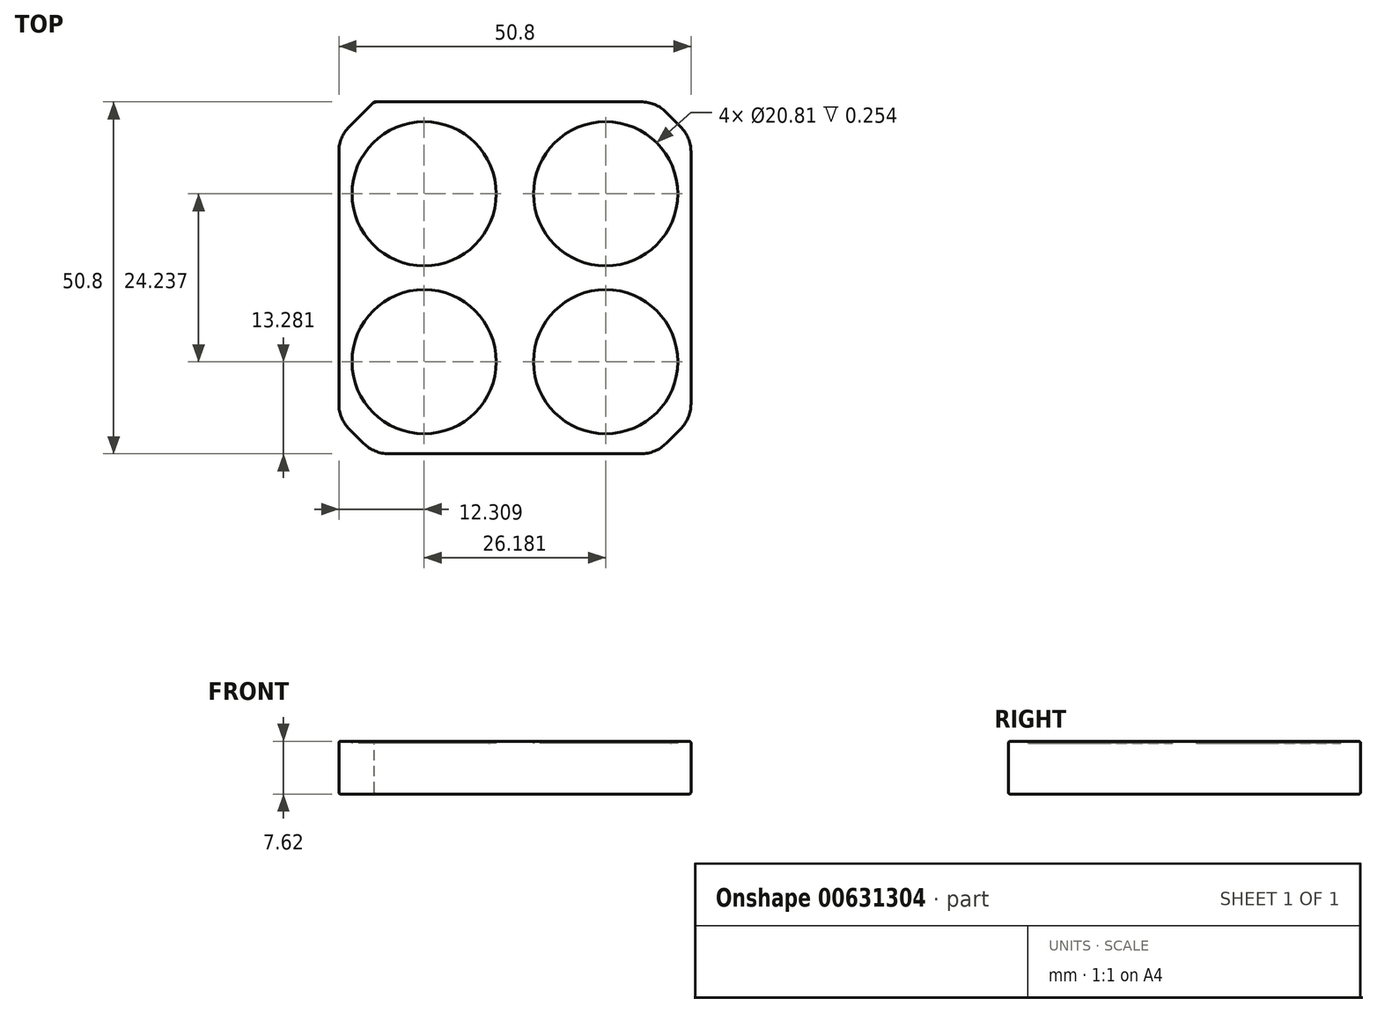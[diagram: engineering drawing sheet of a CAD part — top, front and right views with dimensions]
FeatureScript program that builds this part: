
annotation { "Feature Type Name" : "Feature", "Feature Type Description" : "" }
export const myFeature = defineFeature(function(context is Context, id is Id, definition is map)
    precondition{}
    {
        {
            var Q0;
            Q0=qCreatedBy(makeId("Top.planeOp"),FACE);
            var sketch = newSketch(context, id + "F0", { "sketchPlane" : qUnion([Q0])});
            skLineSegment(sketch, "E0.bottom", {"start": v(-25.4, 25.4) * mm, "end": v(25.4, 25.4) * mm});
            skLineSegment(sketch, "E0.top", {"start": v(-25.4, -25.4) * mm, "end": v(25.4, -25.4) * mm});
            skLineSegment(sketch, "E0.left", {"start": v(-25.4, 25.4) * mm, "end": v(-25.4, -25.4) * mm});
            skLineSegment(sketch, "E0.right", {"start": v(25.4, 25.4) * mm, "end": v(25.4, -25.4) * mm});
            skSolve(sketch);
        }
        {
            var Q0;
            Q0=makeQuery(id+"F0.imprint","IMPRINT",FACE,{"disambiguationData":[TD([[makeQuery(id+"F0.imprint","IMPRINT",EDGE,{"derivedFrom":sQuery(id+"F0.wireOp",EDGE,"E0.bottom")}),-1.0]])]});
            extrude(context, id + "F1", {"entities" : qUnion([Q0]), "depth" : 7.62 * mm, "offsetDistance" : 25.4 * mm});
        }
        {
            var Q0;
            Q0=makeQuery(id+"F1.opExtrude","CAP_FACE",FACE,{"disambiguationData":[OSD([sQuery(id+"F0.wireOp",EDGE,"E0.bottom"),sQuery(id+"F0.wireOp",EDGE,"E0.top"),sQuery(id+"F0.wireOp",EDGE,"E0.left"),sQuery(id+"F0.wireOp",EDGE,"E0.right")])],"isStart":false});
            var sketch = newSketch(context, id + "F2", { "sketchPlane" : qUnion([Q0])});
            skCircle(sketch, "E1", {"center": v(-13.1, 12.12) * mm, "radius": 10.4 * mm});
            skCircle(sketch, "E2.0", {"center": v(-13.1, 12.12) * mm, "radius": 9.13 * mm});
            skCircle(sketch, "E3", {"center": v(13.1, 12.12) * mm, "radius": 10.4 * mm});
            skCircle(sketch, "E4", {"center": v(13.1, 12.12) * mm, "radius": 9.13 * mm});
            skCircle(sketch, "E5", {"center": v(-13.1, -12.12) * mm, "radius": 10.4 * mm});
            skCircle(sketch, "E6", {"center": v(-13.1, -12.12) * mm, "radius": 9.13 * mm});
            skCircle(sketch, "E7", {"center": v(13.1, -12.12) * mm, "radius": 10.4 * mm});
            skCircle(sketch, "E8", {"center": v(13.1, -12.12) * mm, "radius": 9.13 * mm});
            skSolve(sketch);
        }
        {
            var Q0;
            Q0 = qSketchRegion(id + "F2", true);
            extrude(context, id + "F3", {"entities" : qUnion([Q0]), "operationType" : NewBodyOperationType.REMOVE, "oppositeDirection" : true, "depth" : 0.25 * mm, "offsetDistance" : 25.4 * mm});
        }
        {
            var Q0;
            Q0=makeQuery(id+"F1.opExtrude","SWEPT_EDGE",EDGE,{"disambiguationData":[OSD([sQuery(id+"F0.wireOp",EDGE,"E0.top"),sQuery(id+"F0.wireOp",EDGE,"E0.left")])]});
            var Q1;
            Q1=makeQuery(id+"F1.opExtrude","SWEPT_EDGE",EDGE,{"disambiguationData":[OSD([sQuery(id+"F0.wireOp",EDGE,"E0.top"),sQuery(id+"F0.wireOp",EDGE,"E0.right")])]});
            var Q2;
            Q2=makeQuery(id+"F1.opExtrude","SWEPT_EDGE",EDGE,{"disambiguationData":[OSD([sQuery(id+"F0.wireOp",EDGE,"E0.bottom"),sQuery(id+"F0.wireOp",EDGE,"E0.left")])]});
            var Q3;
            Q3=makeQuery(id+"F1.opExtrude","SWEPT_EDGE",EDGE,{"disambiguationData":[OSD([sQuery(id+"F0.wireOp",EDGE,"E0.bottom"),sQuery(id+"F0.wireOp",EDGE,"E0.right")])]});
            chamfer(context, id + "F4", {"entities" : qUnion([Q0, Q1, Q2, Q3]), "width" : 5.08 * mm, "tangentPropagation" : true});
        }
        {
            var Q0;
            Q0=makeQuery(id+"F3.boolean.opBoolean","COPY",EDGE,{"derivedFrom":makeQuery(id+"F3.opExtrude","CAP_EDGE",EDGE,{"disambiguationData":[OSD([sQuery(id+"F2.wireOp",EDGE,"E2.0")])],"isStart":true})});
            var Q1;
            Q1=makeQuery(id+"F3.boolean.opBoolean","COPY",EDGE,{"derivedFrom":makeQuery(id+"F3.opExtrude","CAP_EDGE",EDGE,{"disambiguationData":[OSD([sQuery(id+"F2.wireOp",EDGE,"E1")])],"isStart":true})});
            var Q2;
            Q2=makeQuery(id+"F3.boolean.opBoolean","COPY",EDGE,{"derivedFrom":makeQuery(id+"F3.opExtrude","CAP_EDGE",EDGE,{"disambiguationData":[OSD([sQuery(id+"F2.wireOp",EDGE,"E3")])],"isStart":true})});
            var Q3;
            Q3=makeQuery(id+"F3.boolean.opBoolean","COPY",EDGE,{"derivedFrom":makeQuery(id+"F3.opExtrude","CAP_EDGE",EDGE,{"disambiguationData":[OSD([sQuery(id+"F2.wireOp",EDGE,"E4")])],"isStart":true})});
            var Q4;
            Q4=makeQuery(id+"F3.boolean.opBoolean","COPY",EDGE,{"derivedFrom":makeQuery(id+"F3.opExtrude","CAP_EDGE",EDGE,{"disambiguationData":[OSD([sQuery(id+"F2.wireOp",EDGE,"E7")])],"isStart":true})});
            var Q5;
            Q5=makeQuery(id+"F3.boolean.opBoolean","COPY",EDGE,{"derivedFrom":makeQuery(id+"F3.opExtrude","CAP_EDGE",EDGE,{"disambiguationData":[OSD([sQuery(id+"F2.wireOp",EDGE,"E8")])],"isStart":true})});
            var Q6;
            Q6=makeQuery(id+"F3.boolean.opBoolean","COPY",EDGE,{"derivedFrom":makeQuery(id+"F3.opExtrude","CAP_EDGE",EDGE,{"disambiguationData":[OSD([sQuery(id+"F2.wireOp",EDGE,"E6")])],"isStart":true})});
            var Q7;
            Q7=makeQuery(id+"F3.boolean.opBoolean","COPY",EDGE,{"derivedFrom":makeQuery(id+"F3.opExtrude","CAP_EDGE",EDGE,{"disambiguationData":[OSD([sQuery(id+"F2.wireOp",EDGE,"E5")])],"isStart":true})});
            fillet(context, id + "F5", {"entities" : qUnion([Q0, Q1, Q2, Q3, Q4, Q5, Q6, Q7]), "radius" : 1.27 * mm, "tangentPropagation" : true, "allowEdgeOverflow" : false});
        }
        {
            var Q0;
            {var subQ0=sQuery(id+"F2.wireOp",EDGE,"E1");Q0=makeQuery(id+"F5.opFillet","BLEND_EDGE",EDGE,{"blendedFrom":[makeQuery(id+"F3.boolean.opBoolean","COPY",EDGE,{"derivedFrom":makeQuery(id+"F3.opExtrude","CAP_EDGE",EDGE,{"disambiguationData":[OSD([subQ0])],"isStart":true})}),makeQuery(id+"F3.boolean.opBoolean","COPY",FACE,{"derivedFrom":makeQuery(id+"F3.opExtrude","CAP_FACE",FACE,{"disambiguationData":[OSD([subQ0,sQuery(id+"F2.wireOp",EDGE,"E2.0")])],"isStart":false})})],"blendedInto":[makeQuery(id+"F3.boolean.opBoolean","COPY",FACE,{"derivedFrom":makeQuery(id+"F3.opExtrude","CAP_FACE",FACE,{"disambiguationData":[OSD([subQ0,sQuery(id+"F2.wireOp",EDGE,"E2.0")])],"isStart":false})})]});}
            var Q1;
            {var subQ0=sQuery(id+"F2.wireOp",EDGE,"E2.0");Q1=makeQuery(id+"F5.opFillet","BLEND_EDGE",EDGE,{"blendedFrom":[makeQuery(id+"F3.boolean.opBoolean","COPY",EDGE,{"derivedFrom":makeQuery(id+"F3.opExtrude","CAP_EDGE",EDGE,{"disambiguationData":[OSD([subQ0])],"isStart":true})}),makeQuery(id+"F3.boolean.opBoolean","COPY",FACE,{"derivedFrom":makeQuery(id+"F3.opExtrude","CAP_FACE",FACE,{"disambiguationData":[OSD([sQuery(id+"F2.wireOp",EDGE,"E1"),subQ0])],"isStart":false})})],"blendedInto":[makeQuery(id+"F3.boolean.opBoolean","COPY",FACE,{"derivedFrom":makeQuery(id+"F3.opExtrude","CAP_FACE",FACE,{"disambiguationData":[OSD([sQuery(id+"F2.wireOp",EDGE,"E1"),subQ0])],"isStart":false})})]});}
            var Q2;
            {var subQ0=sQuery(id+"F2.wireOp",EDGE,"E3");Q2=makeQuery(id+"F5.opFillet","BLEND_EDGE",EDGE,{"blendedFrom":[makeQuery(id+"F3.boolean.opBoolean","COPY",EDGE,{"derivedFrom":makeQuery(id+"F3.opExtrude","CAP_EDGE",EDGE,{"disambiguationData":[OSD([subQ0])],"isStart":true})}),makeQuery(id+"F3.boolean.opBoolean","COPY",FACE,{"derivedFrom":makeQuery(id+"F3.opExtrude","CAP_FACE",FACE,{"disambiguationData":[OSD([subQ0,sQuery(id+"F2.wireOp",EDGE,"E4")])],"isStart":false})})],"blendedInto":[makeQuery(id+"F3.boolean.opBoolean","COPY",FACE,{"derivedFrom":makeQuery(id+"F3.opExtrude","CAP_FACE",FACE,{"disambiguationData":[OSD([subQ0,sQuery(id+"F2.wireOp",EDGE,"E4")])],"isStart":false})})]});}
            var Q3;
            {var subQ0=sQuery(id+"F2.wireOp",EDGE,"E4");Q3=makeQuery(id+"F5.opFillet","BLEND_EDGE",EDGE,{"blendedFrom":[makeQuery(id+"F3.boolean.opBoolean","COPY",EDGE,{"derivedFrom":makeQuery(id+"F3.opExtrude","CAP_EDGE",EDGE,{"disambiguationData":[OSD([subQ0])],"isStart":true})}),makeQuery(id+"F3.boolean.opBoolean","COPY",FACE,{"derivedFrom":makeQuery(id+"F3.opExtrude","CAP_FACE",FACE,{"disambiguationData":[OSD([sQuery(id+"F2.wireOp",EDGE,"E3"),subQ0])],"isStart":false})})],"blendedInto":[makeQuery(id+"F3.boolean.opBoolean","COPY",FACE,{"derivedFrom":makeQuery(id+"F3.opExtrude","CAP_FACE",FACE,{"disambiguationData":[OSD([sQuery(id+"F2.wireOp",EDGE,"E3"),subQ0])],"isStart":false})})]});}
            var Q4;
            {var subQ0=sQuery(id+"F2.wireOp",EDGE,"E5");Q4=makeQuery(id+"F5.opFillet","BLEND_EDGE",EDGE,{"blendedFrom":[makeQuery(id+"F3.boolean.opBoolean","COPY",EDGE,{"derivedFrom":makeQuery(id+"F3.opExtrude","CAP_EDGE",EDGE,{"disambiguationData":[OSD([subQ0])],"isStart":false})}),makeQuery(id+"F3.boolean.opBoolean","COPY",FACE,{"derivedFrom":makeQuery(id+"F3.opExtrude","CAP_FACE",FACE,{"disambiguationData":[OSD([subQ0,sQuery(id+"F2.wireOp",EDGE,"E6")])],"isStart":false})})],"blendedInto":[makeQuery(id+"F3.boolean.opBoolean","COPY",FACE,{"derivedFrom":makeQuery(id+"F3.opExtrude","CAP_FACE",FACE,{"disambiguationData":[OSD([subQ0,sQuery(id+"F2.wireOp",EDGE,"E6")])],"isStart":false})})]});}
            var Q5;
            {var subQ0=sQuery(id+"F2.wireOp",EDGE,"E6");Q5=makeQuery(id+"F5.opFillet","BLEND_EDGE",EDGE,{"blendedFrom":[makeQuery(id+"F3.boolean.opBoolean","COPY",EDGE,{"derivedFrom":makeQuery(id+"F3.opExtrude","CAP_EDGE",EDGE,{"disambiguationData":[OSD([subQ0])],"isStart":true})}),makeQuery(id+"F3.boolean.opBoolean","COPY",FACE,{"derivedFrom":makeQuery(id+"F3.opExtrude","CAP_FACE",FACE,{"disambiguationData":[OSD([sQuery(id+"F2.wireOp",EDGE,"E5"),subQ0])],"isStart":false})})],"blendedInto":[makeQuery(id+"F3.boolean.opBoolean","COPY",FACE,{"derivedFrom":makeQuery(id+"F3.opExtrude","CAP_FACE",FACE,{"disambiguationData":[OSD([sQuery(id+"F2.wireOp",EDGE,"E5"),subQ0])],"isStart":false})})]});}
            var Q6;
            {var subQ0=sQuery(id+"F2.wireOp",EDGE,"E7");Q6=makeQuery(id+"F5.opFillet","BLEND_EDGE",EDGE,{"blendedFrom":[makeQuery(id+"F3.boolean.opBoolean","COPY",EDGE,{"derivedFrom":makeQuery(id+"F3.opExtrude","CAP_EDGE",EDGE,{"disambiguationData":[OSD([subQ0])],"isStart":true})}),makeQuery(id+"F3.boolean.opBoolean","COPY",FACE,{"derivedFrom":makeQuery(id+"F3.opExtrude","CAP_FACE",FACE,{"disambiguationData":[OSD([subQ0,sQuery(id+"F2.wireOp",EDGE,"E8")])],"isStart":false})})],"blendedInto":[makeQuery(id+"F3.boolean.opBoolean","COPY",FACE,{"derivedFrom":makeQuery(id+"F3.opExtrude","CAP_FACE",FACE,{"disambiguationData":[OSD([subQ0,sQuery(id+"F2.wireOp",EDGE,"E8")])],"isStart":false})})]});}
            var Q7;
            {var subQ0=sQuery(id+"F2.wireOp",EDGE,"E8");Q7=makeQuery(id+"F5.opFillet","BLEND_EDGE",EDGE,{"blendedFrom":[makeQuery(id+"F3.boolean.opBoolean","COPY",EDGE,{"derivedFrom":makeQuery(id+"F3.opExtrude","CAP_EDGE",EDGE,{"disambiguationData":[OSD([subQ0])],"isStart":true})}),makeQuery(id+"F3.boolean.opBoolean","COPY",FACE,{"derivedFrom":makeQuery(id+"F3.opExtrude","CAP_FACE",FACE,{"disambiguationData":[OSD([sQuery(id+"F2.wireOp",EDGE,"E7"),subQ0])],"isStart":false})})],"blendedInto":[makeQuery(id+"F3.boolean.opBoolean","COPY",FACE,{"derivedFrom":makeQuery(id+"F3.opExtrude","CAP_FACE",FACE,{"disambiguationData":[OSD([sQuery(id+"F2.wireOp",EDGE,"E7"),subQ0])],"isStart":false})})]});}
            var Q8;
            {var subQ0=sQuery(id+"F2.wireOp",EDGE,"E5");Q8=makeQuery(id+"F5.opFillet","BLEND_EDGE",EDGE,{"blendedFrom":[makeQuery(id+"F3.boolean.opBoolean","COPY",EDGE,{"derivedFrom":makeQuery(id+"F3.opExtrude","CAP_EDGE",EDGE,{"disambiguationData":[OSD([subQ0])],"isStart":true})}),makeQuery(id+"F3.boolean.opBoolean","COPY",FACE,{"derivedFrom":makeQuery(id+"F3.opExtrude","CAP_FACE",FACE,{"disambiguationData":[OSD([subQ0,sQuery(id+"F2.wireOp",EDGE,"E6")])],"isStart":false})})],"blendedInto":[makeQuery(id+"F3.boolean.opBoolean","COPY",FACE,{"derivedFrom":makeQuery(id+"F3.opExtrude","CAP_FACE",FACE,{"disambiguationData":[OSD([subQ0,sQuery(id+"F2.wireOp",EDGE,"E6")])],"isStart":false})})]});}
            fillet(context, id + "F6", {"entities" : qUnion([Q0, Q1, Q2, Q3, Q4, Q5, Q6, Q7, Q8]), "radius" : 1.27 * mm, "tangentPropagation" : true, "allowEdgeOverflow" : false});
        }
        {
            var Q0;
            {var subQ0=sQuery(id+"F0.wireOp",EDGE,"E0.left");Q0=makeQuery(id+"F4.opChamfer","BLEND_EDGE",EDGE,{"blendedFrom":[makeQuery(id+"F1.opExtrude","SWEPT_EDGE",EDGE,{"disambiguationData":[OSD([sQuery(id+"F0.wireOp",EDGE,"E0.top"),subQ0])]}),makeQuery(id+"F1.opExtrude","SWEPT_FACE",FACE,{"disambiguationData":[OSD([subQ0])]})],"blendedInto":[makeQuery(id+"F1.opExtrude","SWEPT_FACE",FACE,{"disambiguationData":[OSD([subQ0])]})]});}
            var Q1;
            {var subQ0=sQuery(id+"F0.wireOp",EDGE,"E0.top");Q1=makeQuery(id+"F4.opChamfer","BLEND_EDGE",EDGE,{"blendedFrom":[makeQuery(id+"F1.opExtrude","SWEPT_EDGE",EDGE,{"disambiguationData":[OSD([subQ0,sQuery(id+"F0.wireOp",EDGE,"E0.left")])]}),makeQuery(id+"F1.opExtrude","SWEPT_FACE",FACE,{"disambiguationData":[OSD([subQ0])]})],"blendedInto":[makeQuery(id+"F1.opExtrude","SWEPT_FACE",FACE,{"disambiguationData":[OSD([subQ0])]})]});}
            fillet(context, id + "F7", {"entities" : qUnion([Q0, Q1]), "radius" : 5.08 * mm, "tangentPropagation" : true, "allowEdgeOverflow" : false});
        }
        {
            var Q0;
            {var subQ0=sQuery(id+"F0.wireOp",EDGE,"E0.left");Q0=makeQuery(id+"F4.opChamfer","BLEND_EDGE",EDGE,{"blendedFrom":[makeQuery(id+"F1.opExtrude","SWEPT_EDGE",EDGE,{"disambiguationData":[OSD([sQuery(id+"F0.wireOp",EDGE,"E0.bottom"),subQ0])]}),makeQuery(id+"F1.opExtrude","SWEPT_FACE",FACE,{"disambiguationData":[OSD([subQ0])]})],"blendedInto":[makeQuery(id+"F1.opExtrude","SWEPT_FACE",FACE,{"disambiguationData":[OSD([subQ0])]})]});}
            var Q1;
            {var subQ0=sQuery(id+"F0.wireOp",EDGE,"E0.top");Q1=makeQuery(id+"F4.opChamfer","BLEND_EDGE",EDGE,{"blendedFrom":[makeQuery(id+"F1.opExtrude","SWEPT_EDGE",EDGE,{"disambiguationData":[OSD([subQ0,sQuery(id+"F0.wireOp",EDGE,"E0.right")])]}),makeQuery(id+"F1.opExtrude","SWEPT_FACE",FACE,{"disambiguationData":[OSD([subQ0])]})],"blendedInto":[makeQuery(id+"F1.opExtrude","SWEPT_FACE",FACE,{"disambiguationData":[OSD([subQ0])]})]});}
            var Q2;
            {var subQ0=sQuery(id+"F0.wireOp",EDGE,"E0.right");Q2=makeQuery(id+"F4.opChamfer","BLEND_EDGE",EDGE,{"blendedFrom":[makeQuery(id+"F1.opExtrude","SWEPT_EDGE",EDGE,{"disambiguationData":[OSD([sQuery(id+"F0.wireOp",EDGE,"E0.top"),subQ0])]}),makeQuery(id+"F1.opExtrude","SWEPT_FACE",FACE,{"disambiguationData":[OSD([subQ0])]})],"blendedInto":[makeQuery(id+"F1.opExtrude","SWEPT_FACE",FACE,{"disambiguationData":[OSD([subQ0])]})]});}
            var Q3;
            {var subQ0=sQuery(id+"F0.wireOp",EDGE,"E0.right");Q3=makeQuery(id+"F4.opChamfer","BLEND_EDGE",EDGE,{"blendedFrom":[makeQuery(id+"F1.opExtrude","SWEPT_EDGE",EDGE,{"disambiguationData":[OSD([sQuery(id+"F0.wireOp",EDGE,"E0.bottom"),subQ0])]}),makeQuery(id+"F1.opExtrude","SWEPT_FACE",FACE,{"disambiguationData":[OSD([subQ0])]})],"blendedInto":[makeQuery(id+"F1.opExtrude","SWEPT_FACE",FACE,{"disambiguationData":[OSD([subQ0])]})]});}
            var Q4;
            {var subQ0=sQuery(id+"F0.wireOp",EDGE,"E0.bottom");Q4=makeQuery(id+"F4.opChamfer","BLEND_EDGE",EDGE,{"blendedFrom":[makeQuery(id+"F1.opExtrude","SWEPT_EDGE",EDGE,{"disambiguationData":[OSD([subQ0,sQuery(id+"F0.wireOp",EDGE,"E0.right")])]}),makeQuery(id+"F1.opExtrude","SWEPT_FACE",FACE,{"disambiguationData":[OSD([subQ0])]})],"blendedInto":[makeQuery(id+"F1.opExtrude","SWEPT_FACE",FACE,{"disambiguationData":[OSD([subQ0])]})]});}
            fillet(context, id + "F8", {"entities" : qUnion([Q0, Q1, Q2, Q3, Q4]), "radius" : 5.08 * mm, "tangentPropagation" : true, "allowEdgeOverflow" : false});
        }
        {
            var Q0;
            Q0=makeQuery(id+"F1.opExtrude","CAP_EDGE",EDGE,{"disambiguationData":[OSD([sQuery(id+"F0.wireOp",EDGE,"E0.top")])],"isStart":true});
            var Q1;
            {var subQ0=sQuery(id+"F0.wireOp",EDGE,"E0.left");var subQ1=sQuery(id+"F0.wireOp",EDGE,"E0.top");var subQ2=sQuery(id+"F0.wireOp",EDGE,"E0.right");var subQ3=sQuery(id+"F0.wireOp",EDGE,"E0.bottom");Q1=makeQuery(id+"F4.opChamfer","BLEND_EDGE",EDGE,{"blendedFrom":[makeQuery(id+"F1.opExtrude","SWEPT_EDGE",EDGE,{"disambiguationData":[OSD([subQ1,subQ0])]}),makeQuery(id+"F3.boolean.opBoolean","SPLIT",FACE,{"disambiguationData":[TD([makeQuery(id+"F1.opExtrude","SWEPT_FACE",FACE,{"disambiguationData":[OSD([subQ3])]})])],"derivedFrom":makeQuery(id+"F1.opExtrude","CAP_FACE",FACE,{"disambiguationData":[OSD([subQ3,subQ1,subQ0,subQ2])],"isStart":false})})],"blendedInto":[makeQuery(id+"F3.boolean.opBoolean","SPLIT",FACE,{"disambiguationData":[TD([makeQuery(id+"F1.opExtrude","SWEPT_FACE",FACE,{"disambiguationData":[OSD([subQ3])]})])],"derivedFrom":makeQuery(id+"F1.opExtrude","CAP_FACE",FACE,{"disambiguationData":[OSD([subQ3,subQ1,subQ0,subQ2])],"isStart":false})})]});}
            fillet(context, id + "F9", {"entities" : qUnion([Q0, Q1]), "radius" : 0.25 * mm, "tangentPropagation" : true, "allowEdgeOverflow" : false});
        }
    });
